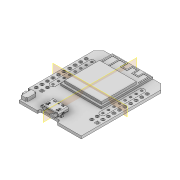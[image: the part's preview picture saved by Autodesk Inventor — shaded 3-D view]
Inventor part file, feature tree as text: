
AUTODESK INVENTOR PART (.ipt)
format: ipt  version: 2022 (Build 260153000, 153)  size: 2,444,800 bytes
history: native  units: mm
features: other x4, plane x2
ambient origin geometry x8: Origin, YZ Plane, XZ Plane, XY Plane, X Axis, Y Axis, Z Axis, Center Point
bodies: Volumenkörper1 (feature_tree), Volumenkörper2 (feature_tree), Volumenkörper3 (feature_tree), Volumenkörper4 (feature_tree)
feature tree (6):
  plane  "Arbeitsebene1"
  plane  "Arbeitsebene2"
  other  "PCB-A-1-solid1"
  other  "PCB-A-1-solid2"
  parser-record x1  (decoder bookkeeping rows leaked as tree rows — omitted from the tree; the rows remain in map.json)
  other  "usb socket1-1-solid1"
